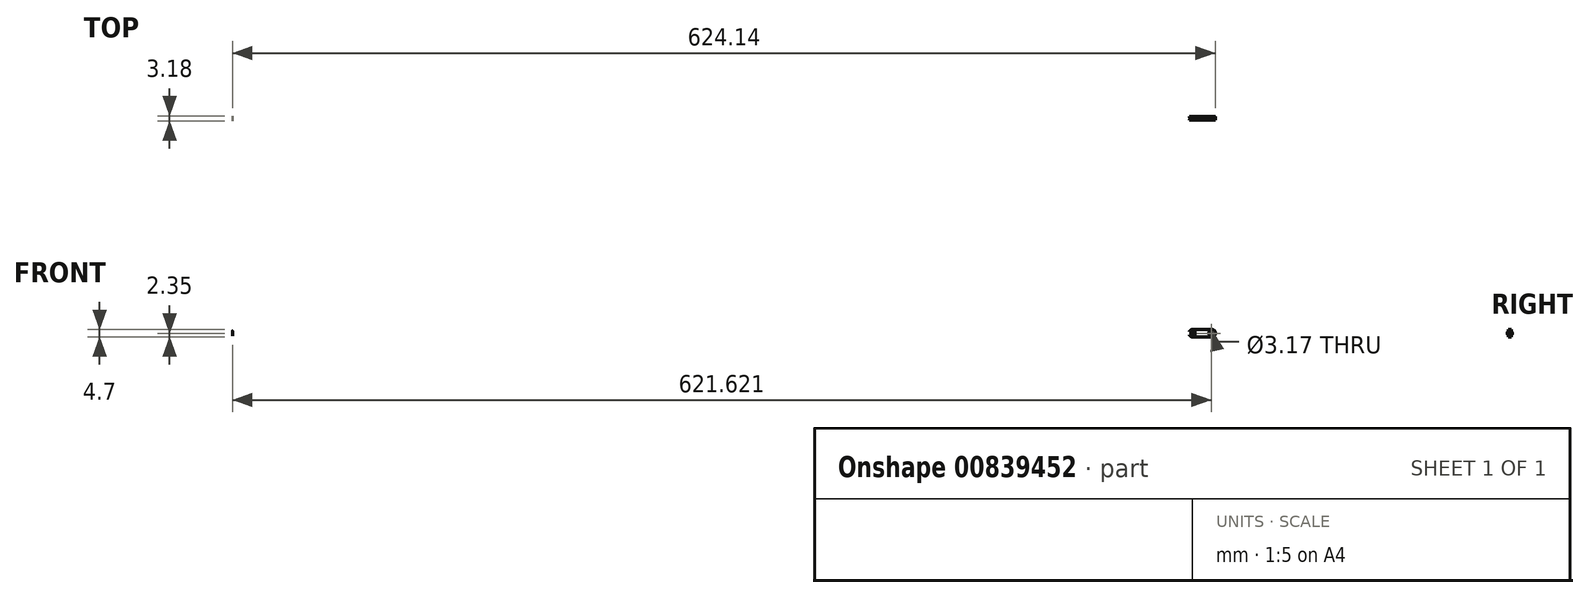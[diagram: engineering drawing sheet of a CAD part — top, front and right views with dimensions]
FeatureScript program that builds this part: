
annotation { "Feature Type Name" : "Feature", "Feature Type Description" : "" }
export const myFeature = defineFeature(function(context is Context, id is Id, definition is map)
    precondition{}
    {
        {
            var Q0;
            Q0=qCreatedBy(makeId("Right.planeOp"),FACE);
            var sketch = newSketch(context, id + "F0", { "sketchPlane" : qUnion([Q0])});
            skCircle(sketch, "E0", {"center": v(0, 0) * mm, "radius": 1.59 * mm});
            skSolve(sketch);
        }
        {
            var Q0;
            Q0 = qSketchRegion(id + "F0", true);
            extrude(context, id + "F1", {"entities" : qUnion([Q0]), "depth" : 609.6 * mm, "offsetDistance" : 25.4 * mm, "symmetric" : true});
        }
        {
            var Q0;
            Q0=qCreatedBy(makeId("Front.planeOp"),FACE);
            var sketch = newSketch(context, id + "F2", { "sketchPlane" : qUnion([Q0])});
            skLineSegment(sketch, "E1.bottom", {"start": v(317.44, -2.35) * mm, "end": v(304.74, -2.35) * mm});
            skLineSegment(sketch, "E1.top", {"start": v(317.44, 2.35) * mm, "end": v(304.74, 2.35) * mm});
            skLineSegment(sketch, "E1.left", {"start": v(319.34, -0.44) * mm, "end": v(319.34, 0.44) * mm});
            skLineSegment(sketch, "E1.right", {"start": v(302.83, -0.44) * mm, "end": v(302.83, 0.44) * mm});
            skPoint(sketch, "E1.middle", {"position": v(311.09, 0) * mm});
            skPoint(sketch, "E2.visualSharp", {"position": v(302.83, 2.35) * mm});
            skArc(sketch, "E2.filletArc", {"start": v(304.74, 2.35) * mm, "mid": v(303.4, 1.79) * mm, "end": v(302.83, 0.44) * mm});
            skPoint(sketch, "E3.visualSharp", {"position": v(302.83, -2.35) * mm});
            skArc(sketch, "E3.filletArc", {"start": v(302.83, -0.44) * mm, "mid": v(303.4, -1.79) * mm, "end": v(304.74, -2.35) * mm});
            skPoint(sketch, "E4.visualSharp", {"position": v(319.34, 2.35) * mm});
            skArc(sketch, "E4.filletArc", {"start": v(319.34, 0.44) * mm, "mid": v(318.79, 1.79) * mm, "end": v(317.44, 2.35) * mm});
            skPoint(sketch, "E5.visualSharp", {"position": v(319.34, -2.35) * mm});
            skArc(sketch, "E5.filletArc", {"start": v(317.44, -2.35) * mm, "mid": v(318.79, -1.79) * mm, "end": v(319.34, -0.44) * mm});
            skSolve(sketch);
        }
        {
            var Q0;
            Q0 = qSketchRegion(id + "F2", true);
            extrude(context, id + "F3", {"entities" : qUnion([Q0]), "operationType" : NewBodyOperationType.ADD, "depth" : 2.16 * mm, "offsetDistance" : 25.4 * mm, "symmetric" : true});
        }
        {
            var Q0;
            Q0=makeQuery(id+"F3.boolean.opBoolean","INTERSECT",EDGE,{"derivedFrom":[makeQuery(id+"F1.opExtrude","CAP_FACE",FACE,{"disambiguationData":[OSD([sQuery(id+"F0.wireOp",EDGE,"E0")])],"isStart":false}),makeQuery(id+"F3.opExtrude","CAP_FACE",FACE,{"disambiguationData":[OSD([sQuery(id+"F2.wireOp",EDGE,"E1.bottom"),sQuery(id+"F2.wireOp",EDGE,"E1.top"),sQuery(id+"F2.wireOp",EDGE,"E1.left"),sQuery(id+"F2.wireOp",EDGE,"E1.right"),sQuery(id+"F2.wireOp",EDGE,"E2.filletArc"),sQuery(id+"F2.wireOp",EDGE,"E3.filletArc"),sQuery(id+"F2.wireOp",EDGE,"E4.filletArc"),sQuery(id+"F2.wireOp",EDGE,"E5.filletArc")])],"isStart":false})]});
            var Q1;
            Q1=makeQuery(id+"F3.boolean.opBoolean","INTERSECT",EDGE,{"derivedFrom":[makeQuery(id+"F1.opExtrude","CAP_FACE",FACE,{"disambiguationData":[OSD([sQuery(id+"F0.wireOp",EDGE,"E0")])],"isStart":false}),makeQuery(id+"F3.opExtrude","CAP_FACE",FACE,{"disambiguationData":[OSD([sQuery(id+"F2.wireOp",EDGE,"E1.bottom"),sQuery(id+"F2.wireOp",EDGE,"E1.top"),sQuery(id+"F2.wireOp",EDGE,"E1.left"),sQuery(id+"F2.wireOp",EDGE,"E1.right"),sQuery(id+"F2.wireOp",EDGE,"E2.filletArc"),sQuery(id+"F2.wireOp",EDGE,"E3.filletArc"),sQuery(id+"F2.wireOp",EDGE,"E4.filletArc"),sQuery(id+"F2.wireOp",EDGE,"E5.filletArc")])],"isStart":true})]});
            fillet(context, id + "F4", {"entities" : qUnion([Q0, Q1]), "tangentPropagation" : true, "radius" : 2.54 * mm, "defaultsChanged" : false, "vertexSettings" : [], "allowEdgeOverflow" : false});
        }
        {
            var Q0;
            Q0=makeQuery(id+"F3.opExtrude","CAP_FACE",FACE,{"disambiguationData":[OSD([sQuery(id+"F2.wireOp",EDGE,"E1.bottom"),sQuery(id+"F2.wireOp",EDGE,"E1.top"),sQuery(id+"F2.wireOp",EDGE,"E1.left"),sQuery(id+"F2.wireOp",EDGE,"E1.right"),sQuery(id+"F2.wireOp",EDGE,"E2.filletArc"),sQuery(id+"F2.wireOp",EDGE,"E3.filletArc"),sQuery(id+"F2.wireOp",EDGE,"E4.filletArc"),sQuery(id+"F2.wireOp",EDGE,"E5.filletArc")])],"isStart":false});
            var sketch = newSketch(context, id + "F5", { "sketchPlane" : qUnion([Q0])});
            skCircle(sketch, "E6", {"center": v(316.82, 0) * mm, "radius": 1.59 * mm});
            skPoint(sketch, "E6.centerSnap0", {"position": v(307.34, 0) * mm});
            skSolve(sketch);
        }
        {
            var Q0;
            Q0 = qSketchRegion(id + "F5", true);
            extrude(context, id + "F6", {"entities" : qUnion([Q0]), "operationType" : NewBodyOperationType.REMOVE, "endBound" : BoundingType.THROUGH_ALL, "oppositeDirection" : true, "depth" : 25.4 * mm, "offsetDistance" : 25.4 * mm});
        }
    });
